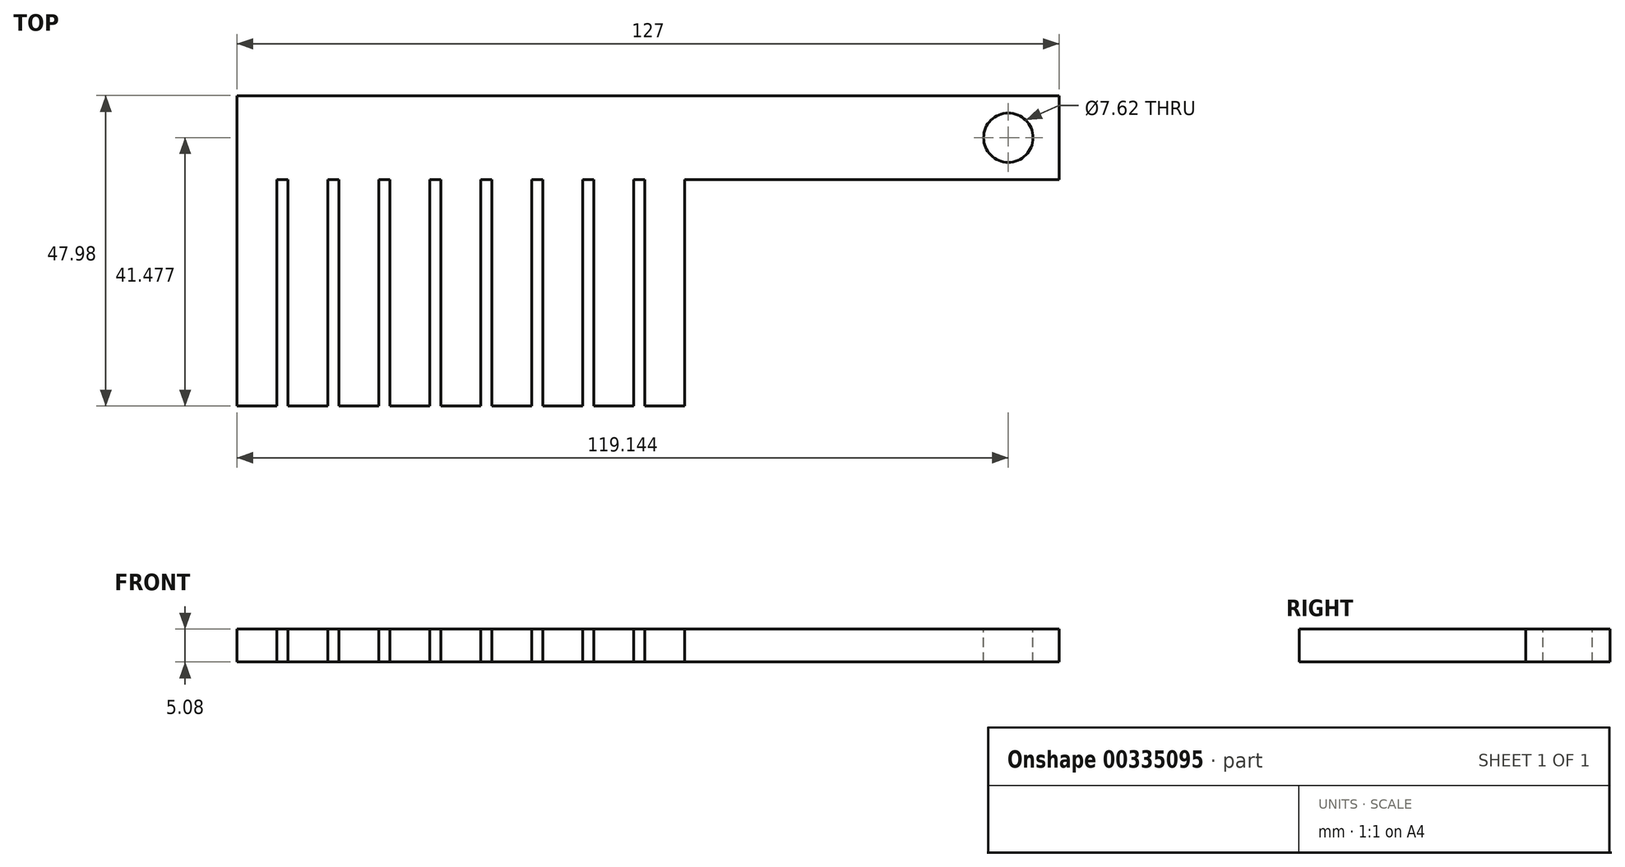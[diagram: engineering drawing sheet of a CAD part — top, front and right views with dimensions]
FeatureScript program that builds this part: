
annotation { "Feature Type Name" : "Feature", "Feature Type Description" : "" }
export const myFeature = defineFeature(function(context is Context, id is Id, definition is map)
    precondition{}
    {
        {
            var Q0;
            Q0=qCreatedBy(makeId("Top.planeOp"),FACE);
            var sketch = newSketch(context, id + "F0", { "sketchPlane" : qUnion([Q0])});
            skLineSegment(sketch, "E0", {"start": v(-111.14, 20.88) * mm, "end": v(15.86, 20.88) * mm});
            skLineSegment(sketch, "E1", {"start": v(15.86, 20.88) * mm, "end": v(15.86, 33.88) * mm});
            skLineSegment(sketch, "E2", {"start": v(15.86, 33.88) * mm, "end": v(-111.14, 33.88) * mm});
            skLineSegment(sketch, "E3", {"start": v(-111.14, 33.88) * mm, "end": v(-111.14, 20.88) * mm});
            skLineSegment(sketch, "E4", {"start": v(-111.14, 20.88) * mm, "end": v(-111.14, -14.1) * mm});
            skLineSegment(sketch, "E5", {"start": v(-111.14, -14.1) * mm, "end": v(-104.97, -14.1) * mm});
            skLineSegment(sketch, "E6", {"start": v(-104.97, -14.1) * mm, "end": v(-104.97, 20.88) * mm});
            skLineSegment(sketch, "E7.1.0.0", {"start": v(-103.26, 20.88) * mm, "end": v(-103.26, -14.1) * mm});
            skLineSegment(sketch, "E7.1.0.1", {"start": v(-103.26, -14.1) * mm, "end": v(-97.1, -14.1) * mm});
            skLineSegment(sketch, "E7.1.0.2", {"start": v(-97.1, -14.1) * mm, "end": v(-97.1, 20.88) * mm});
            skLineSegment(sketch, "E7.2.0.0", {"start": v(-95.39, 20.88) * mm, "end": v(-95.39, -14.1) * mm});
            skLineSegment(sketch, "E7.2.0.1", {"start": v(-95.39, -14.1) * mm, "end": v(-89.23, -14.1) * mm});
            skLineSegment(sketch, "E7.2.0.2", {"start": v(-89.23, -14.1) * mm, "end": v(-89.23, 20.88) * mm});
            skLineSegment(sketch, "E7.3.0.0", {"start": v(-87.51, 20.88) * mm, "end": v(-87.51, -14.1) * mm});
            skLineSegment(sketch, "E7.3.0.1", {"start": v(-87.51, -14.1) * mm, "end": v(-81.35, -14.1) * mm});
            skLineSegment(sketch, "E7.3.0.2", {"start": v(-81.35, -14.1) * mm, "end": v(-81.35, 20.88) * mm});
            skLineSegment(sketch, "E7.4.0.0", {"start": v(-79.64, 20.88) * mm, "end": v(-79.64, -14.1) * mm});
            skLineSegment(sketch, "E7.4.0.1", {"start": v(-79.64, -14.1) * mm, "end": v(-73.48, -14.1) * mm});
            skLineSegment(sketch, "E7.4.0.2", {"start": v(-73.48, -14.1) * mm, "end": v(-73.48, 20.88) * mm});
            skLineSegment(sketch, "E7.5.0.0", {"start": v(-71.77, 20.88) * mm, "end": v(-71.77, -14.1) * mm});
            skLineSegment(sketch, "E7.5.0.1", {"start": v(-71.77, -14.1) * mm, "end": v(-65.6, -14.1) * mm});
            skLineSegment(sketch, "E7.5.0.2", {"start": v(-65.6, -14.1) * mm, "end": v(-65.6, 20.88) * mm});
            skLineSegment(sketch, "E7.6.0.0", {"start": v(-63.9, 20.88) * mm, "end": v(-63.9, -14.1) * mm});
            skLineSegment(sketch, "E7.6.0.1", {"start": v(-63.9, -14.1) * mm, "end": v(-57.73, -14.1) * mm});
            skLineSegment(sketch, "E7.6.0.2", {"start": v(-57.73, -14.1) * mm, "end": v(-57.73, 20.88) * mm});
            skLineSegment(sketch, "E7.7.0.0", {"start": v(-56.02, 20.88) * mm, "end": v(-56.02, -14.1) * mm});
            skLineSegment(sketch, "E7.7.0.1", {"start": v(-56.02, -14.1) * mm, "end": v(-49.86, -14.1) * mm});
            skLineSegment(sketch, "E7.7.0.2", {"start": v(-49.86, -14.1) * mm, "end": v(-49.86, 20.88) * mm});
            skLineSegment(sketch, "E7.8.0.0", {"start": v(-48.14, 20.88) * mm, "end": v(-48.14, -14.1) * mm});
            skLineSegment(sketch, "E7.8.0.1", {"start": v(-48.14, -14.1) * mm, "end": v(-41.98, -14.1) * mm});
            skLineSegment(sketch, "E7.8.0.2", {"start": v(-41.98, -14.1) * mm, "end": v(-41.98, 20.88) * mm});
            skLineSegment(sketch, "E7.direction1", {"start": v(-111.14, -14.1) * mm, "end": v(-103.26, -14.1) * mm, "construction": true});
            skSolve(sketch);
        }
        {
            var Q0;
            Q0 = qSketchRegion(id + "F0", true);
            extrude(context, id + "F1", {"entities" : qUnion([Q0]), "depth" : 5.08 * mm});
        }
        {
            var Q0;
            Q0=makeQuery(id+"F1.opExtrude","CAP_FACE",FACE,{"disambiguationData":[OSD([sQuery(id+"F0.wireOp",EDGE,"E0"),sQuery(id+"F0.wireOp",EDGE,"E1"),sQuery(id+"F0.wireOp",EDGE,"E2"),sQuery(id+"F0.wireOp",EDGE,"E3"),sQuery(id+"F0.wireOp",EDGE,"E4"),sQuery(id+"F0.wireOp",EDGE,"E5"),sQuery(id+"F0.wireOp",EDGE,"E6"),sQuery(id+"F0.wireOp",EDGE,"E7.1.0.0"),sQuery(id+"F0.wireOp",EDGE,"E7.1.0.1"),sQuery(id+"F0.wireOp",EDGE,"E7.1.0.2"),sQuery(id+"F0.wireOp",EDGE,"E7.2.0.0"),sQuery(id+"F0.wireOp",EDGE,"E7.2.0.1"),sQuery(id+"F0.wireOp",EDGE,"E7.2.0.2"),sQuery(id+"F0.wireOp",EDGE,"E7.3.0.0"),sQuery(id+"F0.wireOp",EDGE,"E7.3.0.1"),sQuery(id+"F0.wireOp",EDGE,"E7.3.0.2"),sQuery(id+"F0.wireOp",EDGE,"E7.4.0.0"),sQuery(id+"F0.wireOp",EDGE,"E7.4.0.1"),sQuery(id+"F0.wireOp",EDGE,"E7.4.0.2"),sQuery(id+"F0.wireOp",EDGE,"E7.5.0.0"),sQuery(id+"F0.wireOp",EDGE,"E7.5.0.1"),sQuery(id+"F0.wireOp",EDGE,"E7.5.0.2"),sQuery(id+"F0.wireOp",EDGE,"E7.6.0.0"),sQuery(id+"F0.wireOp",EDGE,"E7.6.0.1"),sQuery(id+"F0.wireOp",EDGE,"E7.6.0.2"),sQuery(id+"F0.wireOp",EDGE,"E7.7.0.0"),sQuery(id+"F0.wireOp",EDGE,"E7.7.0.1"),sQuery(id+"F0.wireOp",EDGE,"E7.7.0.2"),sQuery(id+"F0.wireOp",EDGE,"E7.8.0.0"),sQuery(id+"F0.wireOp",EDGE,"E7.8.0.1"),sQuery(id+"F0.wireOp",EDGE,"E7.8.0.2")])],"isStart":false});
            var sketch = newSketch(context, id + "F2", { "sketchPlane" : qUnion([Q0])});
            skCircle(sketch, "E8", {"center": v(8, 27.38) * mm, "radius": 3.81 * mm});
            skPoint(sketch, "E8.centerSnap0", {"position": v(15.86, 27.38) * mm});
            skSolve(sketch);
        }
        {
            var Q0;
            Q0=makeQuery(id+"F2.imprint","IMPRINT",FACE,{"disambiguationData":[TD([[makeQuery(id+"F2.imprint","IMPRINT",EDGE,{"derivedFrom":sQuery(id+"F2.wireOp",EDGE,"E8")}),1.0]])]});
            extrude(context, id + "F3", {"entities" : qUnion([Q0]), "operationType" : NewBodyOperationType.REMOVE, "oppositeDirection" : true, "depth" : 25.4 * mm});
        }
    });
